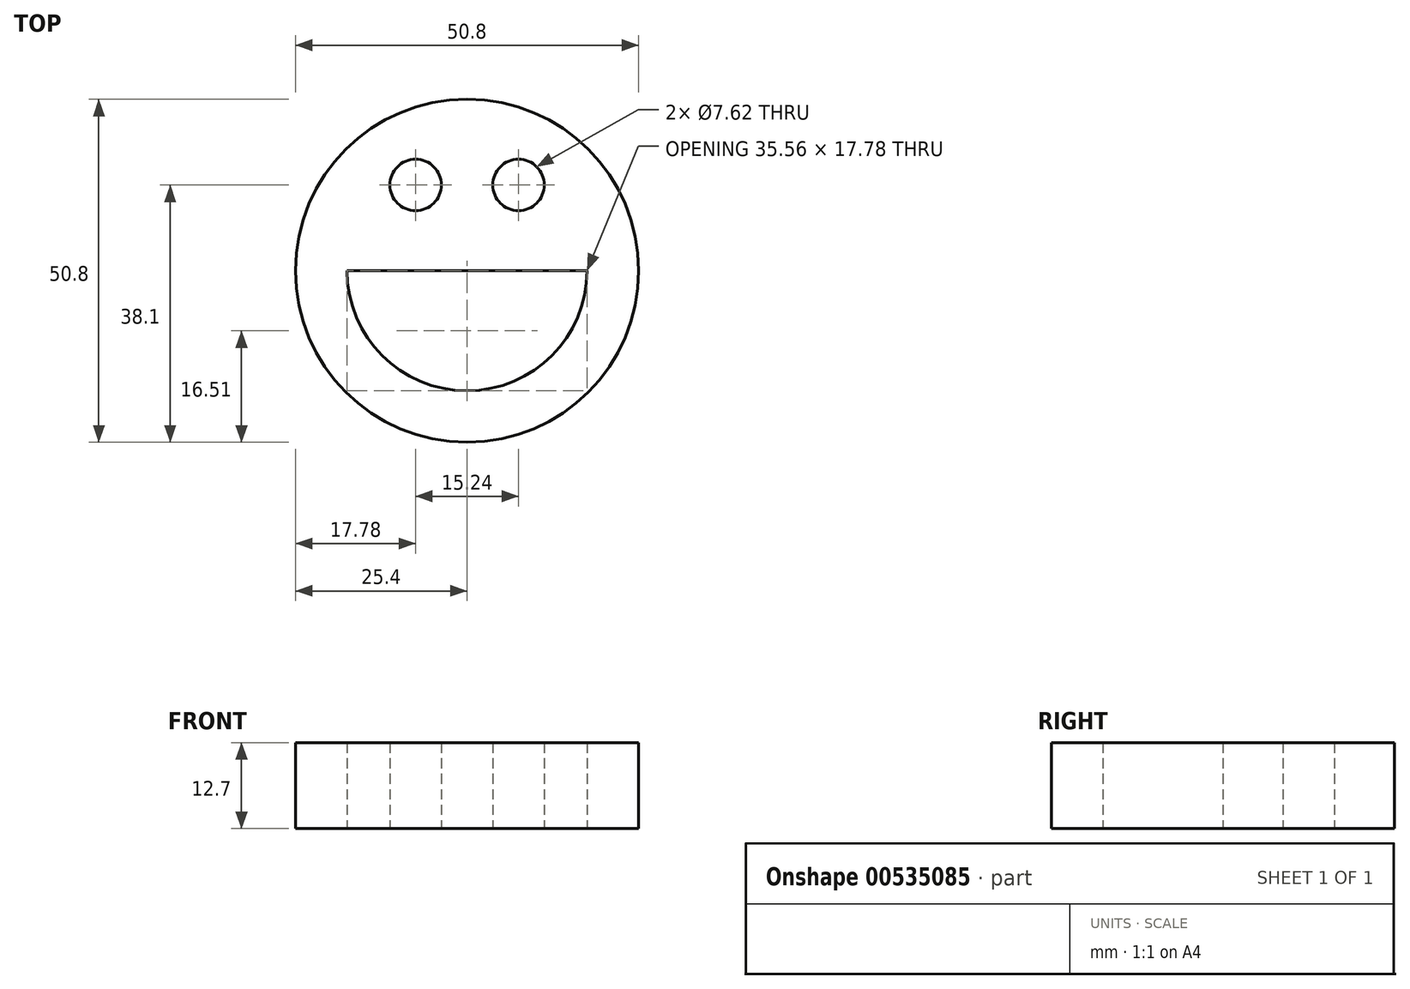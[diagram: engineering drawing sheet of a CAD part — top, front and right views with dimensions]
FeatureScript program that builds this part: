
annotation { "Feature Type Name" : "Feature", "Feature Type Description" : "" }
export const myFeature = defineFeature(function(context is Context, id is Id, definition is map)
    precondition{}
    {
        {
            var Q0;
            Q0=qCreatedBy(makeId("Top.planeOp"),FACE);
            var sketch = newSketch(context, id + "F0", { "sketchPlane" : qUnion([Q0])});
            skCircle(sketch, "E0", {"center": v(0, 0) * mm, "radius": 25.4 * mm});
            skCircle(sketch, "E1", {"center": v(-7.62, 12.7) * mm, "radius": 3.81 * mm});
            skCircle(sketch, "E2", {"center": v(7.62, 12.7) * mm, "radius": 3.81 * mm});
            skArc(sketch, "E3", {"start": v(17.78, 0) * mm, "mid": v(0, -17.78) * mm, "end": v(-17.78, 0) * mm});
            skLineSegment(sketch, "E4", {"start": v(-17.78, 0) * mm, "end": v(17.78, 0) * mm});
            skSolve(sketch);
        }
        {
            var Q0;
            Q0=makeQuery(id+"F0.imprint","IMPRINT",FACE,{"disambiguationData":[TD([[makeQuery(id+"F0.imprint","IMPRINT",EDGE,{"derivedFrom":sQuery(id+"F0.wireOp",EDGE,"E0")}),1.0]])]});
            extrude(context, id + "F1", {"entities" : qUnion([Q0]), "depth" : 12.7 * mm, "offsetDistance" : 25.4 * mm});
        }
    });
